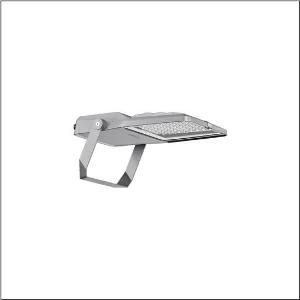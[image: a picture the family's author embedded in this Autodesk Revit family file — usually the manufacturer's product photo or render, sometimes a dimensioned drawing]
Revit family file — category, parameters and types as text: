
# Revit family: floodlight_fl_21_iq_mini___rs12_5xa7771c2b1a_0601
name_source: partatom
category: Lighting Fixtures
units: mm (PartAtom-declared; Revit-internal decimal feet)

## family parameters
Cut with Voids When Loaded = No
Host = Face
Light Source = No
Part Type = Normal
Room Calculation Point = No
Round Connector Dimension = Use Diameter
Shared = No

## types (1)
- --- (1 x LED, 12340 lm, 87.2 W, 3000K)
    Apparent Load = 87 VA
    CIE Flux Codes = 79 92 99 100 100
    Color Rendering = 70
    Color Temperature = 3000K
    Default Elevation = 1800 mm
    Description = Floodlight FL 21 iQ mini, floodlight, primary light control with lens, of PMMA, primary optical cover: protective disc, of toughened safety glass, transparent, light distribution: RS12, light emission: direct distribution, installation type: surface-mounted, lamps: LED, High Power LED, rated values: 12.340lm | 87,2W | 141,5lm/W (begin service life); end service life: 12.340lm | 92,1W; at 50% lumin. flux: 6.170lm | 40,1W | 153,9lm/W, colour temperature: 3000K, colour rendering: CRI > 70, light colour: 730, light setting 1 begin service life: 100% | 12.340lm | 87,2W | 141,5lm/W | 3.000K, light setting 1 end service life: 92,1W, further light settings possible, control: Auto-Match, Temp-Guard, Lumen-Switch, Night-Set, Smart-Wire, Light-Fading, Desk-Remote (wireless, voltage-free reading and setting of iQ features in the workshop via application-optimized NFC function/RFID function), optimised constant luminous flux control (CLO 2.0), pre-setting: linear dimming characteristic, with terminal, 6-pole, mains connection: 220..240V, AC, 50/60Hz, luminaire housing, of diecast aluminium, powder-coated, SITECO metallic grey (DB 702S), corrosivity category C5 mid according to DIN EN ISO 12944suitable for swimming poolschlorine-resistant, sealing non-destructively replaceable, mounting bracket, of steel, galvanised, powder-coated, SITECO metallic grey (DB 702S), protection rating (complete): IP66, insulation class (complete): insulation class II (safety insulation), certification: CE, ENEC, VDE, protection symbol: D, impact resistance: IK08, permissible operating ambient temperature: -40..+40°C, permissible operating ambient temperature for outdoor applications: -40..+50°C, standard: DIN EN 12944, LABS conformity tested according to VDMA 24364:2018-05, packaging unit: 1 piece

Light Distribution: RS12
    Height = 70 mm
    Lamp = 1 x LED
    Lamp Light Flux = 12340 lm
    Lamp Power = 87.2 W
    Lamp count = 1
    Length = 485 mm
    Luminous efficacy = 142 lm/W
    Manufacturer = Siteco
    ModVariant = No
    Model = 5XA7771C2B1A
    Mounting Place = Pole
    Mounting Type = Pole annexe
    Number of Poles = 1
    OnlyDefault = Yes
    Power Factor = 1
    Product Name = Floodlight FL 21 iQ mini | RS12
    Product group = floodlight | pylon annexe
    ProductGroupID = 6201
    Protection Class = Protection class II
    Protection Degree = IP 66
    RLX_Detail_Level = 1
    RLX_Emergency_Light_Flux = 0 lm
    RLX_Emergency_Type = 0
    RLX_Emergency_Type_DB = No
    RlxData = <blob elided: 91365 chars, md5=ae3fd070>
    Socket = socket
    Standby Power = 0 W
    System Light Flux = 12340 lm
    System Power = 87 W
    Type Comments = factory setting: luminous flux: 100 % | dim-lin: 254 | 456 mA
    Type Image = l_1006845.jpg
    URL = http://relux.com
    VarID = @adj_168777
    Voltage = 0 V
    Weight = 0.00 kg
    Width = 337 mm

## geometry (parser evidence)
native form markers: Blend x4, Sweep x15
no freeform markers — native parametric forms only
